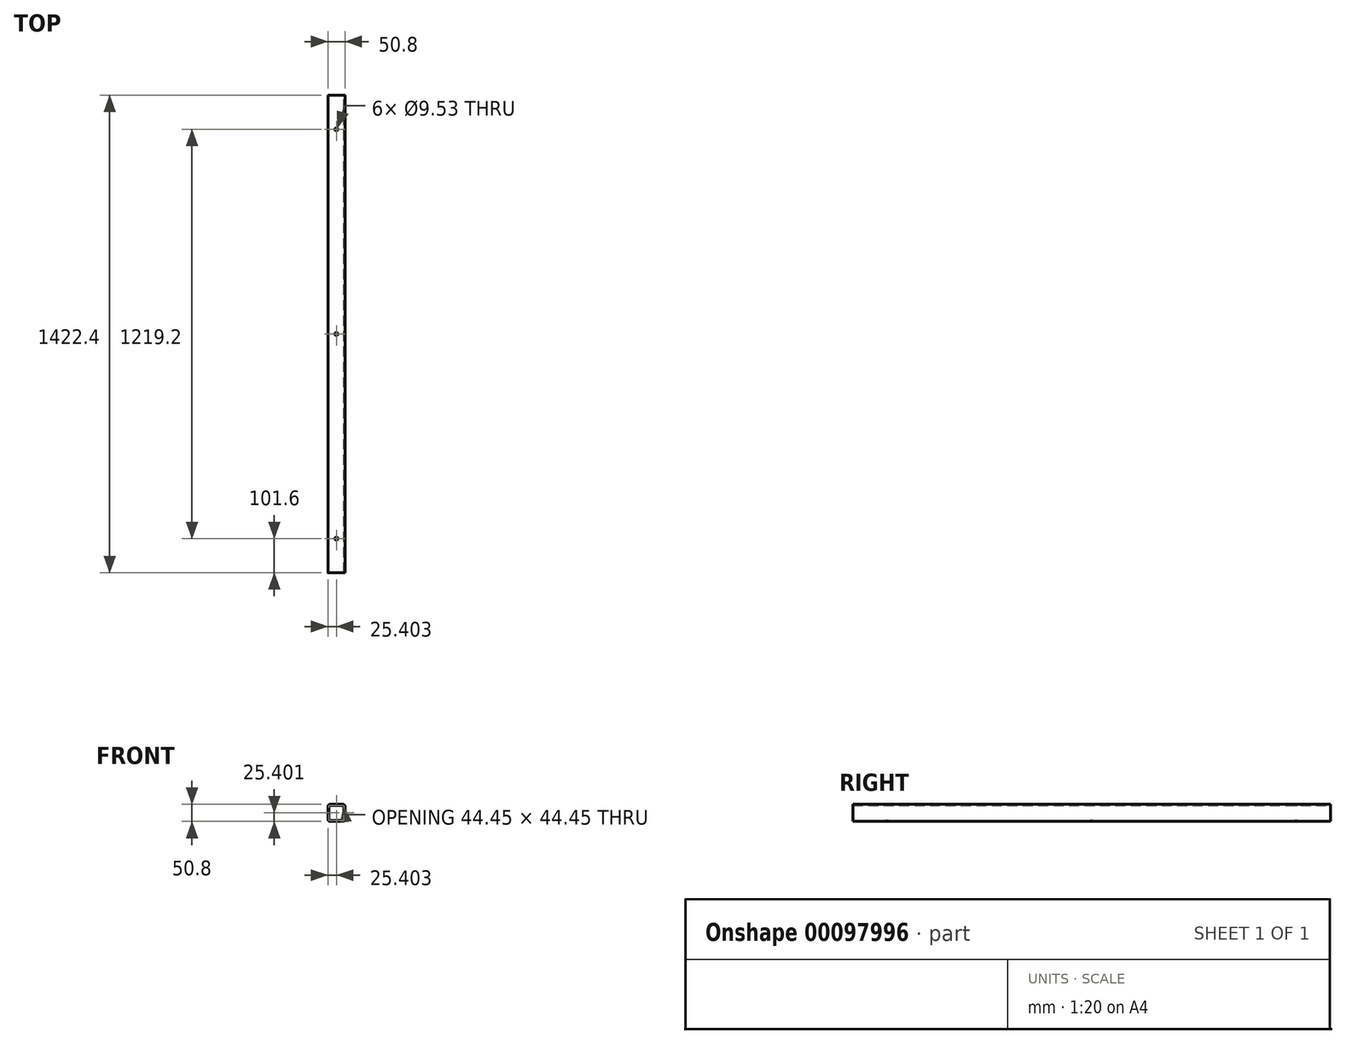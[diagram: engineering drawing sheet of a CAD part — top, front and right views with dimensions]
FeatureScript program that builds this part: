
annotation { "Feature Type Name" : "Feature", "Feature Type Description" : "" }
export const myFeature = defineFeature(function(context is Context, id is Id, definition is map)
    precondition{}
    {
        {
            var Q0;
            Q0=qCreatedBy(makeId("Front.planeOp"),FACE);
            var sketch = newSketch(context, id + "F0", { "sketchPlane" : qUnion([Q0])});
            skLineSegment(sketch, "E0.bottom", {"start": v(19, -25.44) * mm, "end": v(-19.1, -25.44) * mm});
            skLineSegment(sketch, "E0.top", {"start": v(19, 25.36) * mm, "end": v(-19.1, 25.36) * mm});
            skLineSegment(sketch, "E0.left", {"start": v(25.34, -19.09) * mm, "end": v(25.34, 19.01) * mm});
            skLineSegment(sketch, "E0.right", {"start": v(-25.46, -19.09) * mm, "end": v(-25.46, 19.01) * mm});
            skPoint(sketch, "E0.middle", {"position": v(-0.06, -0.04) * mm});
            skLineSegment(sketch, "E1.bottom", {"start": v(19, 22.19) * mm, "end": v(-19.1, 22.19) * mm});
            skLineSegment(sketch, "E1.top", {"start": v(19, -22.26) * mm, "end": v(-19.1, -22.26) * mm});
            skLineSegment(sketch, "E1.left", {"start": v(22.17, 19.01) * mm, "end": v(22.17, -19.09) * mm});
            skLineSegment(sketch, "E1.right", {"start": v(-22.28, 19.01) * mm, "end": v(-22.28, -19.09) * mm});
            skPoint(sketch, "E2.visualSharp", {"position": v(-25.46, 25.36) * mm});
            skArc(sketch, "E2.filletArc", {"start": v(-19.1, 25.36) * mm, "mid": v(-23.6, 23.5) * mm, "end": v(-25.46, 19.01) * mm});
            skPoint(sketch, "E3.visualSharp", {"position": v(25.34, 25.36) * mm});
            skArc(sketch, "E3.filletArc", {"start": v(25.34, 19.01) * mm, "mid": v(23.48, 23.5) * mm, "end": v(19, 25.36) * mm});
            skPoint(sketch, "E4.visualSharp", {"position": v(25.34, -25.44) * mm});
            skArc(sketch, "E4.filletArc", {"start": v(19, -25.44) * mm, "mid": v(23.48, -23.58) * mm, "end": v(25.34, -19.09) * mm});
            skPoint(sketch, "E5.visualSharp", {"position": v(-25.46, -25.44) * mm});
            skArc(sketch, "E5.filletArc", {"start": v(-25.46, -19.09) * mm, "mid": v(-23.6, -23.58) * mm, "end": v(-19.1, -25.44) * mm});
            skPoint(sketch, "E6.visualSharp", {"position": v(22.17, 22.19) * mm});
            skArc(sketch, "E6.filletArc", {"start": v(22.17, 19.01) * mm, "mid": v(21.24, 21.26) * mm, "end": v(19, 22.19) * mm});
            skPoint(sketch, "E7.visualSharp", {"position": v(22.17, -22.26) * mm});
            skArc(sketch, "E7.filletArc", {"start": v(19, -22.26) * mm, "mid": v(21.24, -21.33) * mm, "end": v(22.17, -19.09) * mm});
            skPoint(sketch, "E8.visualSharp", {"position": v(-22.28, -22.26) * mm});
            skArc(sketch, "E8.filletArc", {"start": v(-22.28, -19.09) * mm, "mid": v(-21.35, -21.33) * mm, "end": v(-19.1, -22.26) * mm});
            skPoint(sketch, "E9.visualSharp", {"position": v(-22.28, 22.19) * mm});
            skArc(sketch, "E9.filletArc", {"start": v(-19.1, 22.19) * mm, "mid": v(-21.35, 21.26) * mm, "end": v(-22.28, 19.01) * mm});
            skSolve(sketch);
        }
        {
            var Q0;
            Q0=makeQuery(id+"F0.imprint","IMPRINT",FACE,{"disambiguationData":[TD([[makeQuery(id+"F0.imprint","IMPRINT",EDGE,{"derivedFrom":sQuery(id+"F0.wireOp",EDGE,"E0.bottom")}),-1.0]])]});
            extrude(context, id + "F1", {"entities" : qUnion([Q0]), "endBound" : BoundingType.SYMMETRIC, "depth" : 1422.4 * mm});
        }
        {
            var Q0;
            Q0=makeQuery(id+"F1.opExtrude","SWEPT_FACE",FACE,{"disambiguationData":[OSD([sQuery(id+"F0.wireOp",EDGE,"E0.top")])]});
            var sketch = newSketch(context, id + "F2", { "sketchPlane" : qUnion([Q0])});
            skPoint(sketch, "E10.startSnap0", {"position": v(-19.1, 0) * mm});
            skPoint(sketch, "E10.endSnap0", {"position": v(-19.1, 0) * mm});
            skLineSegment(sketch, "E11", {"start": v(-19.1, 0) * mm, "end": v(19, 0) * mm, "construction": true});
            skCircle(sketch, "E12", {"center": v(-0.06, 0) * mm, "radius": 4.76 * mm});
            skLineSegment(sketch, "E13", {"start": v(-19.1, -609.6) * mm, "end": v(19, -609.6) * mm, "construction": true});
            skLineSegment(sketch, "E14", {"start": v(-0.06, -711.2) * mm, "end": v(-0.06, 711.2) * mm, "construction": true});
            skLineSegment(sketch, "E15", {"start": v(-19.1, 609.6) * mm, "end": v(19, 609.6) * mm, "construction": true});
            skCircle(sketch, "E16", {"center": v(-0.06, 609.6) * mm, "radius": 4.76 * mm});
            skCircle(sketch, "E17", {"center": v(-0.06, -609.6) * mm, "radius": 4.76 * mm});
            skSolve(sketch);
        }
        {
            var Q0;
            Q0=makeQuery(id+"F2.imprint","IMPRINT",FACE,{"disambiguationData":[TD([[makeQuery(id+"F2.imprint","IMPRINT",EDGE,{"derivedFrom":sQuery(id+"F2.wireOp",EDGE,"E17")}),1.0]])]});
            var Q1;
            Q1=makeQuery(id+"F2.imprint","IMPRINT",FACE,{"disambiguationData":[TD([[makeQuery(id+"F2.imprint","IMPRINT",EDGE,{"derivedFrom":sQuery(id+"F2.wireOp",EDGE,"E12")}),1.0]])]});
            var Q2;
            Q2=makeQuery(id+"F2.imprint","IMPRINT",FACE,{"disambiguationData":[TD([[makeQuery(id+"F2.imprint","IMPRINT",EDGE,{"derivedFrom":sQuery(id+"F2.wireOp",EDGE,"E16")}),1.0]])]});
            extrude(context, id + "F3", {"entities" : qUnion([Q0, Q1, Q2]), "operationType" : NewBodyOperationType.REMOVE, "endBound" : BoundingType.THROUGH_ALL, "oppositeDirection" : true, "depth" : 25.4 * mm});
        }
    });
